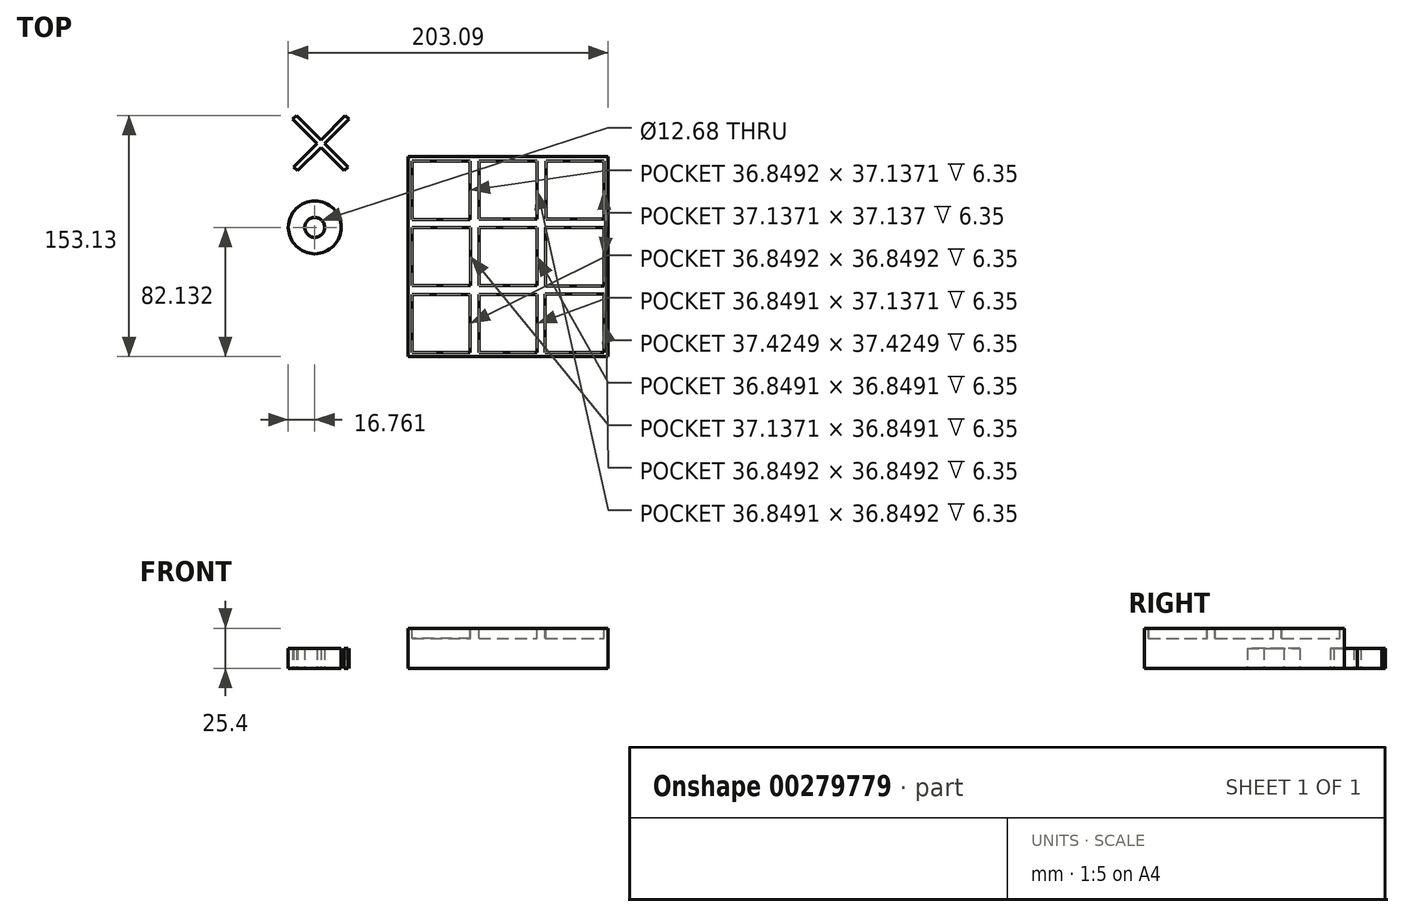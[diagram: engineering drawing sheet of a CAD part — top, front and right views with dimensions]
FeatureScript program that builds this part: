
annotation { "Feature Type Name" : "Feature", "Feature Type Description" : "" }
export const myFeature = defineFeature(function(context is Context, id is Id, definition is map)
    precondition{}
    {
        {
            var Q0;
            Q0=qCreatedBy(makeId("Top.planeOp"),FACE);
            var sketch = newSketch(context, id + "F0", { "sketchPlane" : qUnion([Q0])});
            skLineSegment(sketch, "E0.bottom", {"start": v(-60.77, 50.76) * mm, "end": v(66.23, 50.76) * mm});
            skLineSegment(sketch, "E0.top", {"start": v(-60.77, -76.24) * mm, "end": v(66.23, -76.24) * mm});
            skLineSegment(sketch, "E0.left", {"start": v(-60.77, 50.76) * mm, "end": v(-60.77, -76.24) * mm});
            skLineSegment(sketch, "E0.right", {"start": v(66.23, 50.76) * mm, "end": v(66.23, -76.24) * mm});
            skSolve(sketch);
        }
        {
            var Q0;
            Q0 = qSketchRegion(id + "F0", true);
            extrude(context, id + "F1", {"entities" : qUnion([Q0]), "depth" : 25.4 * mm});
        }
        {
            var Q0;
            Q0=makeQuery(id+"F1.opExtrude","CAP_FACE",FACE,{"disambiguationData":[OSD([sQuery(id+"F0.wireOp",EDGE,"E0.bottom"),sQuery(id+"F0.wireOp",EDGE,"E0.top"),sQuery(id+"F0.wireOp",EDGE,"E0.left"),sQuery(id+"F0.wireOp",EDGE,"E0.right")])],"isStart":false});
            var sketch = newSketch(context, id + "F2", { "sketchPlane" : qUnion([Q0])});
            skLineSegment(sketch, "E1.bottom", {"start": v(-21.3, 10.92) * mm, "end": v(-58.15, 10.92) * mm});
            skLineSegment(sketch, "E1.top", {"start": v(-21.3, 48.06) * mm, "end": v(-58.15, 48.06) * mm});
            skLineSegment(sketch, "E1.left", {"start": v(-21.3, 10.92) * mm, "end": v(-21.3, 48.06) * mm});
            skLineSegment(sketch, "E1.right", {"start": v(-58.15, 10.92) * mm, "end": v(-58.15, 48.06) * mm});
            skLineSegment(sketch, "E2.bottom", {"start": v(-15.83, 11.2) * mm, "end": v(21.02, 11.2) * mm});
            skLineSegment(sketch, "E2.top", {"start": v(-15.83, 48.06) * mm, "end": v(21.02, 48.06) * mm});
            skLineSegment(sketch, "E2.left", {"start": v(-15.83, 11.2) * mm, "end": v(-15.83, 48.06) * mm});
            skLineSegment(sketch, "E2.right", {"start": v(21.02, 11.2) * mm, "end": v(21.02, 48.06) * mm});
            skLineSegment(sketch, "E3.bottom", {"start": v(26.77, 11.2) * mm, "end": v(63.62, 11.2) * mm});
            skLineSegment(sketch, "E3.top", {"start": v(26.77, 48.06) * mm, "end": v(63.62, 48.06) * mm});
            skLineSegment(sketch, "E3.left", {"start": v(26.77, 11.2) * mm, "end": v(26.77, 48.06) * mm});
            skLineSegment(sketch, "E3.right", {"start": v(63.62, 11.2) * mm, "end": v(63.62, 48.06) * mm});
            skLineSegment(sketch, "E4.bottom", {"start": v(-58.15, -31.11) * mm, "end": v(-21.02, -31.11) * mm});
            skLineSegment(sketch, "E4.top", {"start": v(-58.15, 5.74) * mm, "end": v(-21.02, 5.74) * mm});
            skLineSegment(sketch, "E4.left", {"start": v(-58.15, -31.11) * mm, "end": v(-58.15, 5.74) * mm});
            skLineSegment(sketch, "E4.right", {"start": v(-21.02, -31.11) * mm, "end": v(-21.02, 5.74) * mm});
            skLineSegment(sketch, "E5.bottom", {"start": v(-15.83, -31.11) * mm, "end": v(21.02, -31.11) * mm});
            skLineSegment(sketch, "E5.top", {"start": v(-15.83, 5.74) * mm, "end": v(21.02, 5.74) * mm});
            skLineSegment(sketch, "E5.left", {"start": v(-15.83, -31.11) * mm, "end": v(-15.83, 5.74) * mm});
            skLineSegment(sketch, "E5.right", {"start": v(21.02, -31.11) * mm, "end": v(21.02, 5.74) * mm});
            skLineSegment(sketch, "E6.bottom", {"start": v(26.49, -31.4) * mm, "end": v(63.62, -31.4) * mm});
            skLineSegment(sketch, "E6.top", {"start": v(26.49, 5.74) * mm, "end": v(63.62, 5.74) * mm});
            skLineSegment(sketch, "E6.left", {"start": v(26.49, -31.4) * mm, "end": v(26.49, 5.74) * mm});
            skLineSegment(sketch, "E6.right", {"start": v(63.62, -31.4) * mm, "end": v(63.62, 5.74) * mm});
            skLineSegment(sketch, "E7.bottom", {"start": v(-58.15, -73.43) * mm, "end": v(-21.3, -73.43) * mm});
            skLineSegment(sketch, "E7.top", {"start": v(-58.15, -36.58) * mm, "end": v(-21.3, -36.58) * mm});
            skLineSegment(sketch, "E7.left", {"start": v(-58.15, -73.43) * mm, "end": v(-58.15, -36.58) * mm});
            skLineSegment(sketch, "E7.right", {"start": v(-21.3, -73.43) * mm, "end": v(-21.3, -36.58) * mm});
            skLineSegment(sketch, "E8.bottom", {"start": v(-15.83, -73.72) * mm, "end": v(21.02, -73.72) * mm});
            skLineSegment(sketch, "E8.top", {"start": v(-15.83, -36.58) * mm, "end": v(21.02, -36.58) * mm});
            skLineSegment(sketch, "E8.left", {"start": v(-15.83, -73.72) * mm, "end": v(-15.83, -36.58) * mm});
            skLineSegment(sketch, "E8.right", {"start": v(21.02, -73.72) * mm, "end": v(21.02, -36.58) * mm});
            skLineSegment(sketch, "E9.bottom", {"start": v(26.2, -73.72) * mm, "end": v(63.62, -73.72) * mm});
            skLineSegment(sketch, "E9.top", {"start": v(26.2, -36.3) * mm, "end": v(63.62, -36.3) * mm});
            skLineSegment(sketch, "E9.left", {"start": v(26.2, -73.72) * mm, "end": v(26.2, -36.3) * mm});
            skLineSegment(sketch, "E9.right", {"start": v(63.62, -73.72) * mm, "end": v(63.62, -36.3) * mm});
            skSolve(sketch);
        }
        {
            var Q0;
            Q0 = qSketchRegion(id + "F2", true);
            extrude(context, id + "F3", {"entities" : qUnion([Q0]), "operationType" : NewBodyOperationType.REMOVE, "oppositeDirection" : true, "depth" : 6.35 * mm});
        }
        {
            var Q0;
            Q0=qCreatedBy(makeId("Top.planeOp"),FACE);
            var sketch = newSketch(context, id + "F4", { "sketchPlane" : qUnion([Q0])});
            skLineSegment(sketch, "E10", {"start": v(-100.7, 76.9) * mm, "end": v(-133.39, 44.2) * mm});
            skLineSegment(sketch, "E11", {"start": v(-133.39, 44.2) * mm, "end": v(-131.06, 41.88) * mm});
            skLineSegment(sketch, "E12", {"start": v(-131.06, 41.88) * mm, "end": v(-98.37, 74.57) * mm});
            skLineSegment(sketch, "E13", {"start": v(-98.37, 74.57) * mm, "end": v(-100.7, 76.9) * mm});
            skLineSegment(sketch, "E14", {"start": v(-131.69, 76.9) * mm, "end": v(-99, 44.2) * mm});
            skLineSegment(sketch, "E15", {"start": v(-99, 44.2) * mm, "end": v(-101.33, 41.87) * mm});
            skLineSegment(sketch, "E16", {"start": v(-131.69, 76.9) * mm, "end": v(-134.02, 74.56) * mm});
            skLineSegment(sketch, "E17", {"start": v(-134.02, 74.56) * mm, "end": v(-101.33, 41.87) * mm});
            skSolve(sketch);
        }
        {
            var Q0;
            Q0 = qSketchRegion(id + "F4", true);
            extrude(context, id + "F5", {"entities" : qUnion([Q0]), "depth" : 12.7 * mm});
        }
        {
            var Q0;
            Q0=qCreatedBy(makeId("Top.planeOp"),FACE);
            var sketch = newSketch(context, id + "F6", { "sketchPlane" : qUnion([Q0])});
            skCircle(sketch, "E18", {"center": v(-120.1, 5.9) * mm, "radius": 16.76 * mm});
            skCircle(sketch, "E19", {"center": v(-120.1, 5.9) * mm, "radius": 6.34 * mm});
            skSolve(sketch);
        }
        {
            var Q0;
            Q0 = qSketchRegion(id + "F6", true);
            extrude(context, id + "F7", {"entities" : qUnion([Q0]), "depth" : 12.7 * mm});
        }
    });
